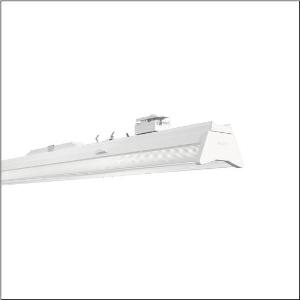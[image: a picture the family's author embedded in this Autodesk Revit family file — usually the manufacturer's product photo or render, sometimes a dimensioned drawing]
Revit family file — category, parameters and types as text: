
# Revit family: licross_r__11_performance_mo_51td16cn49xg_61c3
name_source: partatom
category: Lighting Fixtures
units: mm (PartAtom-declared; Revit-internal decimal feet)

## family parameters
Cut with Voids When Loaded = No
Host = Face
Light Source = No
Part Type = Normal
Room Calculation Point = No
Round Connector Dimension = Use Diameter
Shared = No

## types (1)
- --- (1 x LED, 9190 lm, 49.4 W, 4000K)
    Apparent Load = 49 VA
    CIE Flux Codes = 66 88 96 79 100
    Color Rendering = 80
    Color Temperature = 4000K
    Default Elevation = 1800 mm
    Description = Licross® 11 Performance MO, luminaire insert, of sheet steel, galvanised, coil coated, white, length: 1.500mm, width: 120mm, height: 123mm, LED rated luminous flux: 9.190lm, light colour: 840, control gear: ON/OFF Multilumen, CLOi, with plug, 3-pole, with phase selection, mains connection: 220..240V, AC, 50/60Hz, start of lifetime: 49W, end of service life: 55W, halogen-free wiring, primary light control with lens, of plastic, primary optical cover: cover, of PMMA, light emission: direct/indirect distribution, primary light characteristic: symmetric, protection rating (complete): IP54, insulation class (complete): insulation class I (protective earthing), certification: CE, ENEC, VDE, UKCA, protection symbol: D if used in an environment with non-conductive dust loads with corresponding accessories, impact resistance: IK06, permissible ambient temperature for indoor applications: -35..+40°C, corresponds to IFS (International Featured Standards) requirements for safety and quality in the food industry, reducing of maximum allowable ambient temperature of 5°C with ceiling mounting, LABS conformity tested according to VDMA 24364:2018-05, packaging unit: 1 piece
    Height = 114 mm
    Lamp = 1 x LED
    Lamp Light Flux = 9190 lm
    Lamp Power = 49.4 W
    Lamp count = 1
    Length = 1500 mm
    Luminous efficacy = 186 lm/W
    Manufacturer = Siteco
    ModVariant = No
    Model = 51TD16CN49XG
    Mounting Place = Ceiling
    Mounting Type = Pendant
    Number of Poles = 1
    OnlyDefault = Yes
    Power Factor = 1
    Product Name = Licross® 11 Performance MO
    Product group = luminaire insert
    ProductGroupID = 901
    Protection Class = Protection class I
    Protection Degree = IP 54
    RLX_Detail_Level = 1
    RLX_Emergency_Light_Flux = 0 lm
    RLX_Emergency_Type = 0
    RLX_Emergency_Type_DB = No
    RlxData = <blob elided: 31817 chars, md5=56f4bc8a>
    Socket = socket
    Standby Power = 0 W
    System Light Flux = 9190 lm
    System Power = 49 W
    Type Comments = factory setting: luminous flux: 100 % | (A | C | E) | 113 mA
    Type Image = l_1256138.jpg
    URL = http://relux.com
    VarID = @adj_038271
    Voltage = 0 V
    Weight = 0.00 kg
    Width = 120 mm

## geometry (parser evidence)
native form markers: Blend x4, Sweep x12
no freeform markers — native parametric forms only
